# Revit family: Vitra-BasinGridStrainer-OtherSeries-A45145
name_source: partatom
category: Plumbing Fixtures
revit_build: Autodesk Revit 2017 (Build: 20160225_1515(x64)
units: mm (PartAtom-declared; Revit-internal decimal feet)

## family parameters
Cut with Voids When Loaded = No
Host = Face
OmniClass Number = 23.45.55.17
OmniClass Title = Mixing Faucets
Part Type = Normal
Room Calculation Point = No
Round Connector Dimension = Use Diameter
Shared = Yes

## types (1)
- BasinGridStrainer-Vitra-OtherSeries-A45145
    Article No. (default) = A45145
    BIMobject category = Sanitary - Taps & Mixers
    CW Connection = No
    CWFU = 0
    Coating Material = Vitra-Chrome
    Color = Chrome
    Cost = 0 $
    Default Elevation = 600 mm
    Depth(mm) = 100 mm  [stored 0.328084 ft]
    Design country = Turkey
    HW Connection = No
    HWFU = 0
    Height(mm) = 68 mm
    IFC Classification = Sanitary Terminal
    Manufacturer = Vitra
    Manufacturer name = Vitra
    Masterformat 2014 Code = 22 40 00
    Masterformat 2014 Description = Plumbing Fixtures
    Model = A45145
    MountingType = Pipe Connect
    NBS Referans Code = 62-24
    NBS Referans Description = Drainage Traps
    Nominal height = 0.000
    Nominal width = 0.000
    OmniClass Code = 23-27 37 00
    OmniClass Description = Liquid Traps
    Product SKU = A45145
    Product Type = Basic Grid Strainer
    Product certification = https://vitraglobal.com
    Product data url = https://www.vitra.com.tr
    Product family = OtherSeries
    Product group = Basic Grid Strainer
    Technical description = https://www.vitra.com.tr
    UNSPSC Code = Traps and strainers
    UNSPSC Description = 401425
    URL = https://vitraglobal.com
    Uniclass 1.4 Code = L7254
    Uniclass 1.4 Description = Traps for sinks and basins
    Uniclass 2.0 Code = PR-62-24
    Uniclass 2.0 Description = Drainage Traps
    Uniclass 2015 Code = Pr_65_52_25
    Uniclass 2015 Name = Drainage traps and accessories
    Uniformat II Code = D2010
    Uniformat II Description = Plumbing Fixtures
    WFU = 0
    Warranty Period (Year) = 5
    Waste Connection = Yes
    Weight Net (kg) = 0,338
    Width(mm) = 68 mm
    Youtube = https://www.youtube.com

note: [stored X ft] marks values corroborated as IEEE doubles in the binary element streams (Revit-internal decimal feet)

## geometry (parser evidence)
native form markers: Sweep x3
no freeform markers — native parametric forms only
